# Revit family: PF 22
name_source: partatom
category: Lighting Fixtures
units: mm (PartAtom-declared; Revit-internal decimal feet)

## family parameters
Cut with Voids When Loaded = No
Host = Face
Light Source = Yes
OmniClass Number = 23.80.70.11
OmniClass Title = Luminaries for Internal Lighting
Part Type = Normal
Room Calculation Point = No
Round Connector Dimension = Use Diameter
Shared = No

## types (2) — shared parameters
Beam angle (°) = 110°
Body material = White Powder Coated Aluminium
CRI L'indice di Resa Cromatica = 85
Color Filter = 16777215
Description = La plafoniera PF 22 coniuga le linee geometriche essenziali del quadrato ed un profilo etremamente sottile con fonti luminose LED COB di ultima generazione.
PF 22 può essere impiegata a soffitto o a parete, in ambienti di varia natura come ad esempio alberghi, spazi pubblici o privati, anche con altezze ridotte. Costituisce un'alternativa ai punti luce ad incasso, con notevoli economie di installazione.
Il corpo in pressofusione di alluminio è progettato per garantire la dissipazione passiva del calore generato dal LED. Lo schermo di chiusura è in policarbonato opale ad alta capacità diffondente, e sporge leggermente rispetto al profilo del prodotto, con un effetto luminoso inedito.
Dimming Lamp Color Temperature Shift = <None>
Glass material = Glass
Larghezza = 220 mm
Manufacturer = ARIA
Tilt Angle = 90.00°
Type Comments = Ceiling / Wall light
Type Image = PF 22 ARIA.jpg
URL = https://www.aria.lighting

## per-type parameters (varying)
| type | Codice | Effective Intensity (lm) | Lamp | Model | Photometric Web File | Wattage Comments |
| PF 22 2400lm 18W 3000K CRI85-110° | 3830-01-21 | 1721 | LED 2400lm 18W 3000K CRI85 | 3830-01-21 | 3830-01 _ PF 22 LED 18W 2400 lm.IES | 18 |
| PF 22 3400lm 26W 3000K CRI85-110° | 3831-01-21 | 2479 | LED 3400lm 26W 3000K CRI85 | 3831-01-21 | 3831-01 _ PF 22 LED 26W 3400 lm.IES | 26 |

## geometry (parser evidence)
native form markers: Sweep x3
no freeform markers — native parametric forms only
